# Revit family: Domotics-DomesticRanges-GEWISS-SYSTEM_CLIMATE-BADGE
name_source: partatom
category: Apparecchi elettrici
revit_build: Autodesk Revit 2016 (Build: 20161004_0715(x64)
units: mm (PartAtom-declared; Revit-internal decimal feet)

## family parameters
Condiviso = Sì
Host = Superficie
Mantenere orientamento annotazione = Sì
Punto di calcolo locali = Sì
Quota connettore circolare = Usa diametro
Taglio con vuoti quando caricato = No
Tipo di parte = Normale

## types (2) — shared parameters
Carico apparente = 0 VA
Catalogue = DOMOTICS
Catalogue Range = SYSTEM - DOMESTIC RANGE
Description. = Badge switch
Description: = 1P NO - 10A
Electrocod = 0130
For badge card max. width = 54MM
IDF = 07d50240-89e3-4f70-98c3-3c3d2f852a10
IDT = fd40509d-d89a-4fbe-8451-8eb0a4c867b6
Immagine tipo = GW21820.jpg
N. poli = 1
No. SYSTEM modules = 3
Produttore = GEWISS S.p.A.
Prospetto di default = 1219 mm
SEO = Badge switch
TIPI = System Badge 2M_GENERICO : GW21820 Interruttore badge elettromeccanico 3m nero
Technical sheet = https://www.gewiss.com
Type = Backlit 230V ac
URL = https://www.gewiss.com
Version file RFA = 19.4
Volt = 230 V

## per-type parameters (varying)
| type | Colour | Descrizione | EAN code | Modello | Type: |
| GW21820 - BADGE-OPERATED MECH.SWITCH 3M SY/BK | Black | BADGE-OPERATED MECH.SWITCH 3M SY/BK | 8011564129658 | GW21820 |  |
| GW20820 - BADGE-OPERATED MECH.SWITCH 3M SY/WT | White | BADGE-OPERATED MECH.SWITCH 3M SY/WT | 8011564081161 | GW20820 | Badge |

## geometry (parser evidence)
native form markers: Sweep x1
no freeform markers — native parametric forms only
